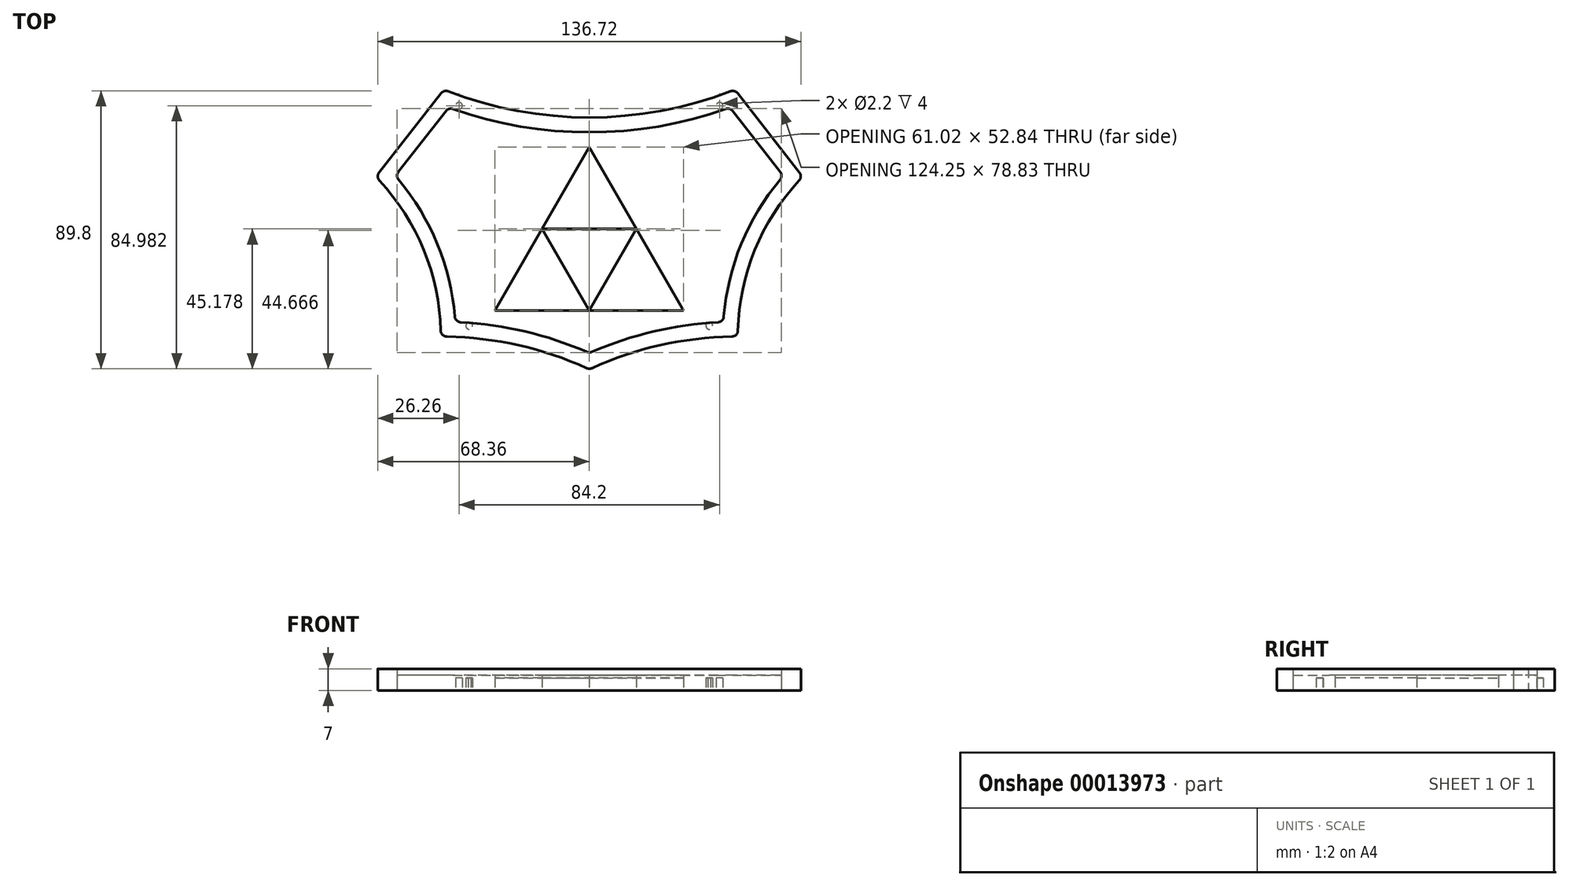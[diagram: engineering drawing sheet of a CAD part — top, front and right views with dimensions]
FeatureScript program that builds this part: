
annotation { "Feature Type Name" : "Feature", "Feature Type Description" : "" }
export const myFeature = defineFeature(function(context is Context, id is Id, definition is map)
    precondition{}
    {
        {
            var Q0;
            Q0=qCreatedBy(makeId("Top.planeOp"),FACE);
            var sketch = newSketch(context, id + "F0", { "sketchPlane" : qUnion([Q0])});
            skLineSegment(sketch, "E0.bottom", {"start": v(0, 0) * mm, "end": v(138, 0) * mm, "construction": true});
            skLineSegment(sketch, "E0.top", {"start": v(0, -90.4) * mm, "end": v(138, -90.4) * mm, "construction": true});
            skLineSegment(sketch, "E0.left", {"start": v(0, 0) * mm, "end": v(0, -90.4) * mm, "construction": true});
            skLineSegment(sketch, "E0.right", {"start": v(138, 0) * mm, "end": v(138, -90.4) * mm, "construction": true});
            skLineSegment(sketch, "E1", {"start": v(21.08, -1.17) * mm, "end": v(1.06, -26.8) * mm});
            skLineSegment(sketch, "E2", {"start": v(116.92, -1.17) * mm, "end": v(136.94, -26.8) * mm});
            skArc(sketch, "E3", {"start": v(23.38, -0.54) * mm, "mid": v(69, -9) * mm, "end": v(114.62, -0.54) * mm});
            skLineSegment(sketch, "E4", {"start": v(69, 0) * mm, "end": v(69, -90.4) * mm, "construction": true});
            skLineSegment(sketch, "E5.0", {"start": v(0, -79.8) * mm, "end": v(135.8, -79.8) * mm, "construction": true});
            skLineSegment(sketch, "E6.0", {"start": v(117, 0) * mm, "end": v(117, -89.2) * mm, "construction": true});
            skArc(sketch, "E7", {"start": v(115.06, -79.82) * mm, "mid": v(91.92, -82.6) * mm, "end": v(69.83, -90.02) * mm});
            skArc(sketch, "E8", {"start": v(136.83, -29.4) * mm, "mid": v(122.5, -51.82) * mm, "end": v(117.03, -77.87) * mm});
            skLineSegment(sketch, "E9.0", {"start": v(21, 0) * mm, "end": v(21, -90.4) * mm, "construction": true});
            skArc(sketch, "E10", {"start": v(68.17, -90.02) * mm, "mid": v(46.08, -82.6) * mm, "end": v(22.94, -79.82) * mm});
            skArc(sketch, "E11", {"start": v(20.97, -77.87) * mm, "mid": v(15.5, -51.82) * mm, "end": v(1.17, -29.4) * mm});
            skLineSegment(sketch, "E12.0", {"start": v(115.3, -6.89) * mm, "end": v(130.7, -26.61) * mm});
            skArc(sketch, "E13.0", {"start": v(130.65, -29.13) * mm, "mid": v(118.13, -49.82) * mm, "end": v(112.47, -73.34) * mm});
            skArc(sketch, "E14.0", {"start": v(110.58, -75.17) * mm, "mid": v(89.76, -78.17) * mm, "end": v(69.8, -84.78) * mm});
            skLineSegment(sketch, "E15.0", {"start": v(22.7, -6.89) * mm, "end": v(7.3, -26.61) * mm});
            skArc(sketch, "E16.0", {"start": v(25.53, -73.34) * mm, "mid": v(19.87, -49.82) * mm, "end": v(7.35, -29.13) * mm});
            skArc(sketch, "E17.0", {"start": v(68.2, -84.78) * mm, "mid": v(48.24, -78.17) * mm, "end": v(27.42, -75.17) * mm});
            skArc(sketch, "E18.trimOffspring", {"start": v(24.95, -6.24) * mm, "mid": v(69, -13.8) * mm, "end": v(113.05, -6.24) * mm});
            skPoint(sketch, "E19.first.point", {"position": v(69, -13.8) * mm});
            skPoint(sketch, "E19.second.point", {"position": v(58.2, -80.98) * mm});
            skPoint(sketch, "E19.third.point", {"position": v(79.8, -80.98) * mm});
            skLineSegment(sketch, "E20", {"start": v(69, -53.83) * mm, "end": v(69, -18.6) * mm, "construction": true});
            skLineSegment(sketch, "E21.1.0", {"start": v(69, -53.83) * mm, "end": v(38.5, -71.44) * mm, "construction": true});
            skLineSegment(sketch, "E21.2.0", {"start": v(69, -53.83) * mm, "end": v(99.5, -71.44) * mm, "construction": true});
            skPoint(sketch, "E21.center", {"position": v(69, -53.83) * mm});
            skLineSegment(sketch, "E22", {"start": v(69, -18.6) * mm, "end": v(38.5, -71.44) * mm});
            skLineSegment(sketch, "E23", {"start": v(38.5, -71.44) * mm, "end": v(99.5, -71.44) * mm});
            skLineSegment(sketch, "E24", {"start": v(99.5, -71.44) * mm, "end": v(69, -18.6) * mm});
            skLineSegment(sketch, "E25", {"start": v(53.75, -45.02) * mm, "end": v(69, -71.44) * mm});
            skLineSegment(sketch, "E26", {"start": v(69, -71.44) * mm, "end": v(84.25, -45.02) * mm});
            skLineSegment(sketch, "E27", {"start": v(84.25, -45.02) * mm, "end": v(53.75, -45.02) * mm});
            skArc(sketch, "E28.0", {"start": v(112.15, -70.3) * mm, "mid": v(89.11, -73.39) * mm, "end": v(67.06, -80.74) * mm, "construction": true});
            skArc(sketch, "E29.0", {"start": v(70.94, -80.74) * mm, "mid": v(48.89, -73.39) * mm, "end": v(25.85, -70.3) * mm, "construction": true});
            skArc(sketch, "E30.0", {"start": v(21.95, -10.26) * mm, "mid": v(69, -18.6) * mm, "end": v(116.05, -10.26) * mm, "construction": true});
            skPoint(sketch, "E31.visualSharp", {"position": v(22, 0) * mm});
            skArc(sketch, "E31.filletArc", {"start": v(23.38, -0.54) * mm, "mid": v(22.12, -0.48) * mm, "end": v(21.08, -1.17) * mm});
            skPoint(sketch, "E32.visualSharp", {"position": v(0, -28.16) * mm});
            skArc(sketch, "E32.filletArc", {"start": v(1.06, -26.8) * mm, "mid": v(0.64, -28.12) * mm, "end": v(1.17, -29.4) * mm});
            skPoint(sketch, "E33.visualSharp", {"position": v(21, -79.8) * mm});
            skArc(sketch, "E33.filletArc", {"start": v(20.97, -77.87) * mm, "mid": v(21.57, -79.24) * mm, "end": v(22.94, -79.82) * mm});
            skPoint(sketch, "E34.visualSharp", {"position": v(69, -90.4) * mm});
            skArc(sketch, "E34.filletArc", {"start": v(68.17, -90.02) * mm, "mid": v(69, -90.2) * mm, "end": v(69.83, -90.02) * mm});
            skPoint(sketch, "E35.visualSharp", {"position": v(117, -79.8) * mm});
            skArc(sketch, "E35.filletArc", {"start": v(115.06, -79.82) * mm, "mid": v(116.43, -79.24) * mm, "end": v(117.03, -77.87) * mm});
            skPoint(sketch, "E36.visualSharp", {"position": v(138, -28.16) * mm});
            skArc(sketch, "E36.filletArc", {"start": v(136.83, -29.4) * mm, "mid": v(137.36, -28.12) * mm, "end": v(136.94, -26.8) * mm});
            skPoint(sketch, "E37.visualSharp", {"position": v(116, 0) * mm});
            skArc(sketch, "E37.filletArc", {"start": v(116.92, -1.17) * mm, "mid": v(115.88, -0.48) * mm, "end": v(114.62, -0.54) * mm});
            skPoint(sketch, "E38.visualSharp", {"position": v(23.6, -5.75) * mm});
            skArc(sketch, "E38.filletArc", {"start": v(24.95, -6.24) * mm, "mid": v(23.72, -6.2) * mm, "end": v(22.7, -6.89) * mm});
            skPoint(sketch, "E39.visualSharp", {"position": v(6.3, -27.9) * mm});
            skArc(sketch, "E39.filletArc", {"start": v(7.3, -26.61) * mm, "mid": v(6.88, -27.88) * mm, "end": v(7.35, -29.13) * mm});
            skPoint(sketch, "E40.visualSharp", {"position": v(25.66, -75.1) * mm});
            skArc(sketch, "E40.filletArc", {"start": v(25.53, -73.34) * mm, "mid": v(26.13, -74.61) * mm, "end": v(27.42, -75.17) * mm});
            skPoint(sketch, "E41.visualSharp", {"position": v(69, -85.13) * mm});
            skArc(sketch, "E41.filletArc", {"start": v(68.2, -84.78) * mm, "mid": v(69, -84.95) * mm, "end": v(69.8, -84.78) * mm});
            skPoint(sketch, "E42.visualSharp", {"position": v(112.34, -75.1) * mm});
            skArc(sketch, "E42.filletArc", {"start": v(110.58, -75.17) * mm, "mid": v(111.87, -74.61) * mm, "end": v(112.47, -73.34) * mm});
            skPoint(sketch, "E43.visualSharp", {"position": v(131.7, -27.9) * mm});
            skArc(sketch, "E43.filletArc", {"start": v(130.65, -29.13) * mm, "mid": v(131.12, -27.88) * mm, "end": v(130.7, -26.61) * mm});
            skPoint(sketch, "E44.visualSharp", {"position": v(114.4, -5.75) * mm});
            skArc(sketch, "E44.filletArc", {"start": v(115.3, -6.89) * mm, "mid": v(114.28, -6.2) * mm, "end": v(113.05, -6.24) * mm});
            skSolve(sketch);
        }
        {
            var Q0;
            Q0=makeQuery(id+"F0.imprint","IMPRINT",FACE,{"disambiguationData":[TD([[makeQuery(id+"F0.imprint","IMPRINT",EDGE,{"derivedFrom":sQuery(id+"F0.wireOp",EDGE,"E1")}),1.0]])]});
            extrude(context, id + "F1", {"entities" : qUnion([Q0]), "depth" : 7 * mm});
        }
        {
            var Q0;
            Q0=makeQuery(id+"F0.imprint","IMPRINT",FACE,{"disambiguationData":[TD([[makeQuery(id+"F0.imprint","IMPRINT",EDGE,{"derivedFrom":sQuery(id+"F0.wireOp",EDGE,"E12.0")}),-1.0]])]});
            var Q1;
            Q1=makeQuery(id+"F0.imprint","IMPRINT",FACE,{"disambiguationData":[TD([[makeQuery(id+"F0.imprint","IMPRINT",EDGE,{"derivedFrom":sQuery(id+"F0.wireOp",EDGE,"E25")}),1.0]])]});
            extrude(context, id + "F2", {"entities" : qUnion([Q0, Q1]), "depth" : 5 * mm});
        }
        {
            var Q0;
            {var subQ0=sQuery(id+"F0.wireOp",EDGE,"E25");Q0=makeQuery(id+"F0.imprint","IMPRINT",FACE,{"disambiguationData":[TD([[makeQuery(id+"F0.imprint","IMPRINT",EDGE,{"derivedFrom":subQ0}),-1.0]])]});}
            var Q1;
            {var subQ0=sQuery(id+"F0.wireOp",EDGE,"E27");Q1=makeQuery(id+"F0.imprint","IMPRINT",FACE,{"disambiguationData":[TD([[makeQuery(id+"F0.imprint","IMPRINT",EDGE,{"derivedFrom":subQ0}),-1.0]])]});}
            var Q2;
            {var subQ0=sQuery(id+"F0.wireOp",EDGE,"E26");Q2=makeQuery(id+"F0.imprint","IMPRINT",FACE,{"disambiguationData":[TD([[makeQuery(id+"F0.imprint","IMPRINT",EDGE,{"derivedFrom":subQ0}),-1.0]])]});}
            extrude(context, id + "F3", {"entities" : qUnion([Q0, Q1, Q2]), "depth" : 4 * mm});
        }
        {
            var Q0;
            Q0=makeQuery(id+"F0.imprint","IMPRINT",FACE,{"disambiguationData":[TD([[makeQuery(id+"F0.imprint","IMPRINT",EDGE,{"derivedFrom":sQuery(id+"F0.wireOp",EDGE,"E12.0")}),-1.0]])]});
            var sketch = newSketch(context, id + "F4", { "sketchPlane" : qUnion([Q0])});
            skLineSegment(sketch, "E45.0", {"start": v(69, 0) * mm, "end": v(69, -90.4) * mm, "construction": true});
            skArc(sketch, "E46.0", {"start": v(24.95, -6.24) * mm, "mid": v(69, -13.8) * mm, "end": v(113.05, -6.24) * mm});
            skArc(sketch, "E47.0", {"start": v(23.38, -0.54) * mm, "mid": v(69, -9) * mm, "end": v(114.62, -0.54) * mm});
            skArc(sketch, "E48.0", {"start": v(22.23, -3.53) * mm, "mid": v(69, -12.2) * mm, "end": v(115.77, -3.53) * mm, "construction": true});
            skLineSegment(sketch, "E49.0", {"start": v(26.9, 0) * mm, "end": v(26.9, -90.4) * mm, "construction": true});
            skLineSegment(sketch, "E50.0", {"start": v(111.1, 0) * mm, "end": v(111.1, -90.4) * mm, "construction": true});
            skCircle(sketch, "E51", {"center": v(26.9, -5.22) * mm, "radius": 1.1 * mm});
            skCircle(sketch, "E52", {"center": v(111.1, -5.22) * mm, "radius": 1.1 * mm});
            skArc(sketch, "E53.0", {"start": v(68.2, -84.78) * mm, "mid": v(48.24, -78.17) * mm, "end": v(27.42, -75.17) * mm});
            skArc(sketch, "E54.0", {"start": v(110.58, -75.17) * mm, "mid": v(89.76, -78.17) * mm, "end": v(69.8, -84.78) * mm});
            skArc(sketch, "E55.0", {"start": v(68.17, -90.02) * mm, "mid": v(46.08, -82.6) * mm, "end": v(22.94, -79.82) * mm});
            skArc(sketch, "E56.0", {"start": v(115.06, -79.82) * mm, "mid": v(91.92, -82.6) * mm, "end": v(69.83, -90.02) * mm});
            skArc(sketch, "E57.0", {"start": v(69.74, -86.56) * mm, "mid": v(46.92, -78.89) * mm, "end": v(23, -76.02) * mm, "construction": true});
            skArc(sketch, "E58.0", {"start": v(115, -76.02) * mm, "mid": v(91.08, -78.89) * mm, "end": v(68.26, -86.56) * mm, "construction": true});
            skLineSegment(sketch, "E59.0", {"start": v(30.2, 0) * mm, "end": v(30.2, -90.4) * mm, "construction": true});
            skLineSegment(sketch, "E60.0", {"start": v(107.8, 0) * mm, "end": v(107.8, -90.4) * mm, "construction": true});
            skCircle(sketch, "E61", {"center": v(30.2, -76.36) * mm, "radius": 1.1 * mm});
            skCircle(sketch, "E62", {"center": v(107.8, -76.36) * mm, "radius": 1.1 * mm});
            skSolve(sketch);
        }
        {
            var Q0;
            Q0 = qSketchRegion(id + "F4", true);
            extrude(context, id + "F5", {"entities" : qUnion([Q0]), "operationType" : NewBodyOperationType.REMOVE, "depth" : 4 * mm});
        }
    });
